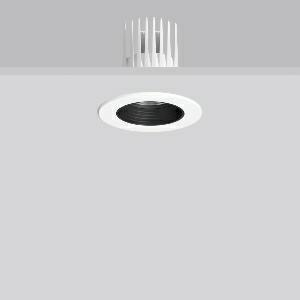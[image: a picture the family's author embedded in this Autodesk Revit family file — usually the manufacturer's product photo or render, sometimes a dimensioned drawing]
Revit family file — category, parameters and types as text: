
# Revit family: heledon_mini_e_901752_002_2_e040
name_source: partatom
category: Lighting Fixtures
units: mm (PartAtom-declared; Revit-internal decimal feet)

## family parameters
Cut with Voids When Loaded = No
Host = Face
Light Source = No
Part Type = Normal
Room Calculation Point = No
Round Connector Dimension = Use Diameter
Shared = No

## types (1)
- HELEDON mini E (1 x LED Modul 927, 2850 lm, 2700)
    Apparent Load = 29 VA
    Approval mark = CE
    CIE Flux Codes = 96 100 100 100 100
    Color Rendering = 92
    Color Temperature = 2700
    Default Elevation = 1800 mm
    Description = Series: HELEDON mini
Round recessed downlight. Housing: die-cast aluminium, powder-coated. Black plastic ring and recessed LED to prevent glare from the side. Optical assembly with lens made of plastic (polycarbonate) for the best homogeneous light distribution - can be changed without tools. Best colour rendering index Ra>90. Suitable for Recessed ceiling mounting. Installation without tools thanks to spring fastening system. Including separate LED converter with connecting cable 600 mm.High quality converter without flickering and stroboscopic effect. Through-wiring box (5 pole) available as accessory. The following accessories can be mounted without use of tools: interchangeable lenses, decorative glasses, honeycomb louvre, clear and frosted diffusers, white interchangeable plastic ring. 
Colour: traffic white, matt (RAL 9016)
Diameter: 124 mm
Height: 3 mm
Cut-out diameter: 114 mm
Recess height: 170 mm
Luminaire: recess height: 120 mm
Lamp: LED
Socket: without socket
Colour temperature: 2700K
Colour rendering index (CRI): 92
System power: 29 W
Rated luminous flux: 2850 lm
Luminous efficiency: 98 lm/W
Control gear: Regulated power supply
Protection class: II
Type of protection: IP 20
    Height = 0 mm  [stored 0 ft]
    Lamp = 1 x LED Modul 927
    Lamp Light Flux = 2850 lm
    Lamp count = 1
    Length = 124 mm  [stored 0.406824 ft]
    Lifetime = 50000 h
    Luminous efficacy = 98 lm/W
    Manufacturer = RZB
    ModVariant = No
    Model = 901752.002.2
    Mounting Place = Ceiling
    Mounting Type = Recessed
    Number of Poles = 1
    OnlyDefault = Yes
    Power Factor = 1
    Product Name = HELEDON mini E
    Product group = Recessed downlights
    ProductGroupID = 402
    Protection Class = Protection class II
    Protection Degree = IP 20
    RLX_Detail_Level = 1
    RLX_Emergency_Light_Flux = 0 lm
    RLX_Emergency_Type = 0
    RLX_Emergency_Type_DB = No
    RlxData = <blob elided: 123889 chars, md5=b918bf48>
    Socket = socket
    Standby Power = 0 W
    System Light Flux = 2850 lm
    System Power = 29 W
    Type Comments = Product without accessories
    Type Image = 901656.002.jpg
    URL = http://relux.com
    VarID = ---
    Voltage = 230 V
    Voltage Range = 220-240 V
    Weight = 0.00 kg
    Width = 0 mm  [stored 0 ft]

note: [stored X ft] marks values corroborated as IEEE doubles in the binary element streams (Revit-internal decimal feet)

## geometry (parser evidence)
native form markers: Blend x4, Sweep x13
no freeform markers — native parametric forms only
